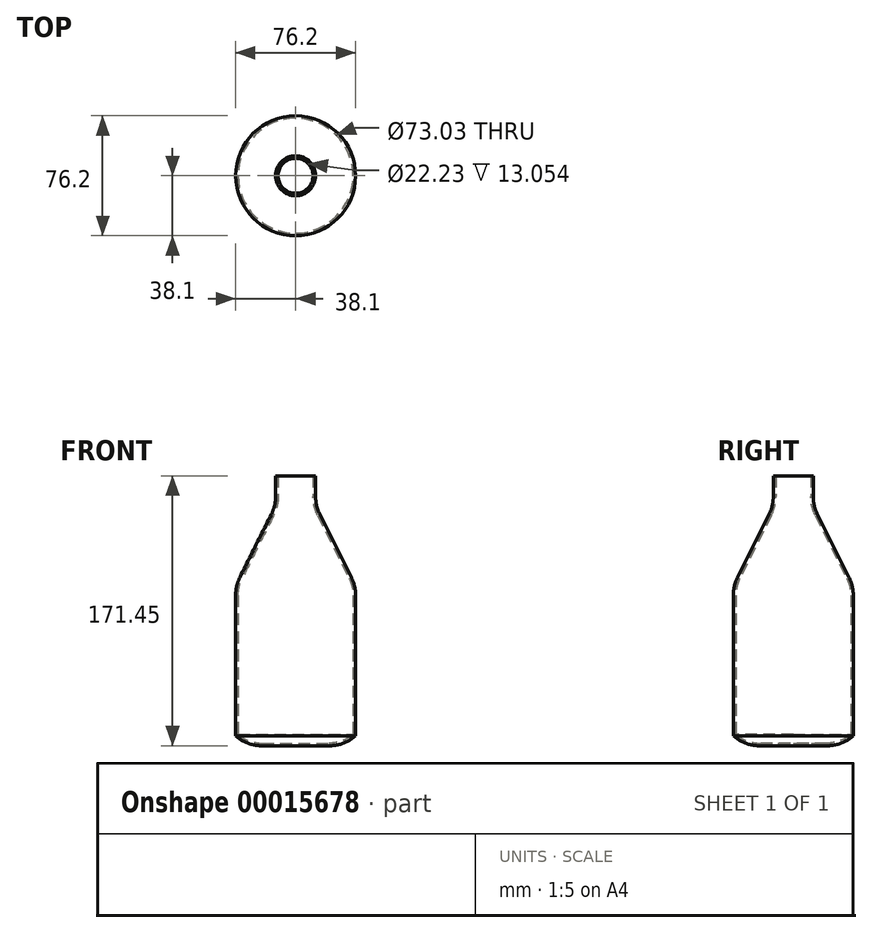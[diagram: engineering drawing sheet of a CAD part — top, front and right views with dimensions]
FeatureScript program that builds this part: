
annotation { "Feature Type Name" : "Feature", "Feature Type Description" : "" }
export const myFeature = defineFeature(function(context is Context, id is Id, definition is map)
    precondition{}
    {
        {
            var Q0;
            Q0=qCreatedBy(makeId("Top.planeOp"),FACE);
            var sketch = newSketch(context, id + "F0", { "sketchPlane" : qUnion([Q0])});
            skCircle(sketch, "E0", {"center": v(0, 0) * mm, "radius": 38.1 * mm});
            skSolve(sketch);
        }
        {
            var Q0;
            Q0 = qSketchRegion(id + "F0", true);
            extrude(context, id + "F1", {"entities" : qUnion([Q0]), "depth" : 152.4 * mm});
        }
        {
            var Q0;
            Q0=makeQuery(id+"F1.opExtrude","CAP_FACE",FACE,{"disambiguationData":[OSD([sQuery(id+"F0.wireOp",EDGE,"E0")])],"isStart":false});
            var sketch = newSketch(context, id + "F2", { "sketchPlane" : qUnion([Q0])});
            skCircle(sketch, "E1", {"center": v(0, 0) * mm, "radius": 12.7 * mm});
            skSolve(sketch);
        }
        {
            var Q0;
            Q0 = qSketchRegion(id + "F2", true);
            extrude(context, id + "F3", {"entities" : qUnion([Q0]), "operationType" : NewBodyOperationType.ADD, "depth" : 19.05 * mm});
        }
        {
            var Q0;
            Q0=makeQuery(id+"F1.opExtrude","CAP_EDGE",EDGE,{"disambiguationData":[OSD([sQuery(id+"F0.wireOp",EDGE,"E0")])],"isStart":false});
            chamfer(context, id + "F4", {"entities" : qUnion([Q0]), "chamferType" : ChamferType.TWO_OFFSETS, "width1" : 25.4 * mm, "oppositeDirection" : false, "width2" : 50.8 * mm, "tangentPropagation" : true});
        }
        {
            var Q0;
            Q0=makeQuery(id+"F1.opExtrude","CAP_EDGE",EDGE,{"disambiguationData":[OSD([sQuery(id+"F0.wireOp",EDGE,"E0")])],"isStart":true});
            chamfer(context, id + "F5", {"entities" : qUnion([Q0]), "width" : 6.35 * mm, "tangentPropagation" : true});
        }
        {
            var Q0;
            Q0=makeQuery(id+"F4.opChamfer","BLEND_FACE",FACE,{"disambiguationData":[OSD([sQuery(id+"F0.wireOp",EDGE,"E0")])]});
            var Q1;
            {var subQ0=sQuery(id+"F0.wireOp",EDGE,"E0");Q1=makeQuery(id+"F5.opChamfer","BLEND_EDGE",EDGE,{"blendedFrom":[makeQuery(id+"F1.opExtrude","CAP_EDGE",EDGE,{"disambiguationData":[OSD([subQ0])],"isStart":true}),makeQuery(id+"F1.opExtrude","CAP_FACE",FACE,{"disambiguationData":[OSD([subQ0])],"isStart":true})],"blendedInto":[makeQuery(id+"F1.opExtrude","CAP_FACE",FACE,{"disambiguationData":[OSD([subQ0])],"isStart":true})]});}
            fillet(context, id + "F6", {"entities" : qUnion([Q0, Q1]), "radius" : 25.4 * mm, "tangentPropagation" : true, "allowEdgeOverflow" : false});
        }
        {
            var Q0;
            Q0=makeQuery(id+"F3.opExtrude","CAP_FACE",FACE,{"disambiguationData":[OSD([sQuery(id+"F2.wireOp",EDGE,"E1")])],"isStart":false});
            shell(context, id + "F7", {"entities" : qUnion([Q0]), "thickness" : 1.59 * mm});
        }
    });
